FCSTD DOCUMENT  (FreeCAD 0.20R26155 (Git))
Label: helical-antenna 300-500MHz
License: All rights reserved
LicenseURL: http://en.wikipedia.org/wiki/All_rights_reserved
objects: Sketcher::SketchObject×1
note: 1 computed .brp shape members not serialized (recipe doc carries the construction recipe); baked Part::Feature solids carry a one-line shape summary decoded from their .brp

FEATURE [Sketcher::SketchObject] Sketch  label="Pads_TH_SMD"
  FullyConstrained = true
  sketch-geometry (95):
    g0: ArcOfCircle CenterX=0.508 CenterY=0.508 CenterZ=0 NormalX=0 NormalY=0 NormalZ=1 AngleXU=0 Radius=0.508 StartAngle=2.89823 EndAngle=6.03983
    g1: ArcOfCircle CenterX=1.524 CenterY=4.60016 CenterZ=0 NormalX=0 NormalY=0 NormalZ=1 AngleXU=0 Radius=0.508 StartAngle=6.03983 EndAngle=9.18142
    g2: LineSegment StartX=1.00103 StartY=0.38559 StartZ=0 EndX=2.01703 EndY=4.47775 EndZ=0
    g3: LineSegment StartX=1.03097 StartY=4.72257 StartZ=0 EndX=0.0149687 EndY=0.63041 EndZ=0
    g4: LineSegment StartX=0.38559 StartY=0.0149687 StartZ=0 EndX=1.64641 EndY=5.09319 EndZ=0
    g5: ArcOfCircle CenterX=2.54 CenterY=0.508 CenterZ=0 NormalX=0 NormalY=0 NormalZ=1 AngleXU=0 Radius=0.508 StartAngle=2.89823 EndAngle=6.03983
    g6: ArcOfCircle CenterX=3.556 CenterY=4.60016 CenterZ=0 NormalX=0 NormalY=0 NormalZ=1 AngleXU=0 Radius=0.508 StartAngle=6.03983 EndAngle=9.18142
    g7: LineSegment StartX=3.03303 StartY=0.38559 StartZ=0 EndX=4.04903 EndY=4.47775 EndZ=0
    g8: LineSegment StartX=3.06297 StartY=4.72257 StartZ=0 EndX=2.04697 EndY=0.63041 EndZ=0
    g9: LineSegment StartX=2.41759 StartY=0.0149687 StartZ=0 EndX=3.67841 EndY=5.09319 EndZ=0
    g10: LineSegment StartX=0.0149687 StartY=0.63041 StartZ=0 EndX=2.04697 EndY=0.63041 EndZ=0
    g11: ArcOfCircle CenterX=4.572 CenterY=0.508 CenterZ=0 NormalX=0 NormalY=0 NormalZ=1 AngleXU=0 Radius=0.508 StartAngle=2.89823 EndAngle=6.03983
    g12: ArcOfCircle CenterX=5.588 CenterY=4.60016 CenterZ=0 NormalX=0 NormalY=0 NormalZ=1 AngleXU=0 Radius=0.508 StartAngle=6.03983 EndAngle=9.18142
    g13: LineSegment StartX=5.06503 StartY=0.38559 StartZ=0 EndX=6.08103 EndY=4.47775 EndZ=0
    g14: LineSegment StartX=5.09497 StartY=4.72257 StartZ=0 EndX=4.07897 EndY=0.63041 EndZ=0
    g15: LineSegment StartX=4.44959 StartY=0.0149687 StartZ=0 EndX=5.71041 EndY=5.09319 EndZ=0
    g16: LineSegment StartX=2.04697 StartY=0.63041 StartZ=0 EndX=4.07897 EndY=0.63041 EndZ=0
    g17: ArcOfCircle CenterX=6.604 CenterY=0.508 CenterZ=0 NormalX=0 NormalY=0 NormalZ=1 AngleXU=0 Radius=0.508 StartAngle=2.89823 EndAngle=6.03983
    g18: ArcOfCircle CenterX=7.62 CenterY=4.60016 CenterZ=0 NormalX=0 NormalY=0 NormalZ=1 AngleXU=0 Radius=0.508 StartAngle=6.03983 EndAngle=9.18142
    g19: LineSegment StartX=7.09703 StartY=0.38559 StartZ=0 EndX=8.11303 EndY=4.47775 EndZ=0
    g20: LineSegment StartX=7.12697 StartY=4.72257 StartZ=0 EndX=6.11097 EndY=0.63041 EndZ=0
    g21: LineSegment StartX=6.48159 StartY=0.0149687 StartZ=0 EndX=7.74241 EndY=5.09319 EndZ=0
    g22: LineSegment StartX=4.07897 StartY=0.63041 StartZ=0 EndX=6.11097 EndY=0.63041 EndZ=0
    g23: ArcOfCircle CenterX=8.636 CenterY=0.508 CenterZ=0 NormalX=0 NormalY=0 NormalZ=1 AngleXU=0 Radius=0.508 StartAngle=2.89823 EndAngle=6.03983
    g24: ArcOfCircle CenterX=9.652 CenterY=4.60016 CenterZ=0 NormalX=0 NormalY=0 NormalZ=1 AngleXU=0 Radius=0.508 StartAngle=6.03983 EndAngle=9.18142
    g25: LineSegment StartX=9.12903 StartY=0.38559 StartZ=0 EndX=10.145 EndY=4.47775 EndZ=0
    g26: LineSegment StartX=9.15897 StartY=4.72257 StartZ=0 EndX=8.14297 EndY=0.63041 EndZ=0
    g27: LineSegment StartX=8.51359 StartY=0.0149687 StartZ=0 EndX=9.77441 EndY=5.09319 EndZ=0
    g28: LineSegment StartX=6.11097 StartY=0.63041 StartZ=0 EndX=8.14297 EndY=0.63041 EndZ=0
    g29: ArcOfCircle CenterX=10.668 CenterY=0.508 CenterZ=0 NormalX=0 NormalY=0 NormalZ=1 AngleXU=0 Radius=0.508 StartAngle=2.89823 EndAngle=6.03983
    g30: ArcOfCircle CenterX=11.684 CenterY=4.60016 CenterZ=0 NormalX=0 NormalY=0 NormalZ=1 AngleXU=0 Radius=0.508 StartAngle=6.03983 EndAngle=9.18142
    g31: LineSegment StartX=11.161 StartY=0.38559 StartZ=0 EndX=12.177 EndY=4.47775 EndZ=0
    g32: LineSegment StartX=11.191 StartY=4.72257 StartZ=0 EndX=10.175 EndY=0.63041 EndZ=0
    g33: LineSegment StartX=10.5456 StartY=0.0149687 StartZ=0 EndX=11.8064 EndY=5.09319 EndZ=0
    g34: LineSegment StartX=8.14297 StartY=0.63041 StartZ=0 EndX=10.175 EndY=0.63041 EndZ=0
    g35: ArcOfCircle CenterX=12.7 CenterY=0.508 CenterZ=0 NormalX=0 NormalY=0 NormalZ=1 AngleXU=0 Radius=0.508 StartAngle=2.89823 EndAngle=6.03983
    g36: ArcOfCircle CenterX=13.716 CenterY=4.60016 CenterZ=0 NormalX=0 NormalY=0 NormalZ=1 AngleXU=0 Radius=0.508 StartAngle=6.03983 EndAngle=9.18142
    g37: LineSegment StartX=13.193 StartY=0.38559 StartZ=0 EndX=14.209 EndY=4.47775 EndZ=0
    g38: LineSegment StartX=13.223 StartY=4.72257 StartZ=0 EndX=12.207 EndY=0.63041 EndZ=0
    g39: LineSegment StartX=12.5776 StartY=0.0149687 StartZ=0 EndX=13.8384 EndY=5.09319 EndZ=0
    g40: LineSegment StartX=10.175 StartY=0.63041 StartZ=0 EndX=12.207 EndY=0.63041 EndZ=0
    g41: ArcOfCircle CenterX=14.732 CenterY=0.508 CenterZ=0 NormalX=0 NormalY=0 NormalZ=1 AngleXU=0 Radius=0.508 StartAngle=2.89823 EndAngle=6.03983
    g42: ArcOfCircle CenterX=15.748 CenterY=4.60016 CenterZ=0 NormalX=0 NormalY=0 NormalZ=1 AngleXU=0 Radius=0.508 StartAngle=6.03983 EndAngle=9.18142
    g43: LineSegment StartX=15.225 StartY=0.38559 StartZ=0 EndX=16.241 EndY=4.47775 EndZ=0
    g44: LineSegment StartX=15.255 StartY=4.72257 StartZ=0 EndX=14.239 EndY=0.63041 EndZ=0
    g45: LineSegment StartX=14.6096 StartY=0.0149687 StartZ=0 EndX=15.8704 EndY=5.09319 EndZ=0
    g46: LineSegment StartX=12.207 StartY=0.63041 StartZ=0 EndX=14.239 EndY=0.63041 EndZ=0
    g47: ArcOfCircle CenterX=16.764 CenterY=0.508 CenterZ=0 NormalX=0 NormalY=0 NormalZ=1 AngleXU=0 Radius=0.508 StartAngle=2.89823 EndAngle=6.03983
    g48: ArcOfCircle CenterX=17.78 CenterY=4.60016 CenterZ=0 NormalX=0 NormalY=0 NormalZ=1 AngleXU=0 Radius=0.508 StartAngle=6.03983 EndAngle=9.18142
    g49: LineSegment StartX=17.257 StartY=0.38559 StartZ=0 EndX=18.273 EndY=4.47775 EndZ=0
    g50: LineSegment StartX=17.287 StartY=4.72257 StartZ=0 EndX=16.271 EndY=0.63041 EndZ=0
    g51: LineSegment StartX=16.6416 StartY=0.0149687 StartZ=0 EndX=17.9024 EndY=5.09319 EndZ=0
    g52: LineSegment StartX=14.239 StartY=0.63041 StartZ=0 EndX=16.271 EndY=0.63041 EndZ=0
    g53: ArcOfCircle CenterX=18.796 CenterY=0.508 CenterZ=0 NormalX=0 NormalY=0 NormalZ=1 AngleXU=0 Radius=0.508 StartAngle=2.89823 EndAngle=6.03983
    g54: ArcOfCircle CenterX=19.812 CenterY=4.60016 CenterZ=0 NormalX=0 NormalY=0 NormalZ=1 AngleXU=0 Radius=0.508 StartAngle=6.03983 EndAngle=9.18142
    g55: LineSegment StartX=19.289 StartY=0.38559 StartZ=0 EndX=20.305 EndY=4.47775 EndZ=0
    g56: LineSegment StartX=19.319 StartY=4.72257 StartZ=0 EndX=18.303 EndY=0.63041 EndZ=0
    g57: LineSegment StartX=18.6736 StartY=0.0149687 StartZ=0 EndX=19.9344 EndY=5.09319 EndZ=0
    g58: LineSegment StartX=16.271 StartY=0.63041 StartZ=0 EndX=18.303 EndY=0.63041 EndZ=0
    g59: ArcOfCircle CenterX=20.828 CenterY=0.508 CenterZ=0 NormalX=0 NormalY=0 NormalZ=1 AngleXU=0 Radius=0.508 StartAngle=2.89823 EndAngle=6.03983
    g60: ArcOfCircle CenterX=21.844 CenterY=4.60016 CenterZ=0 NormalX=0 NormalY=0 NormalZ=1 AngleXU=0 Radius=0.508 StartAngle=6.03983 EndAngle=9.18142
    g61: LineSegment StartX=21.321 StartY=0.38559 StartZ=0 EndX=22.337 EndY=4.47775 EndZ=0
    g62: LineSegment StartX=21.351 StartY=4.72257 StartZ=0 EndX=20.335 EndY=0.63041 EndZ=0
    g63: LineSegment StartX=20.7056 StartY=0.0149687 StartZ=0 EndX=21.9664 EndY=5.09319 EndZ=0
    g64: LineSegment StartX=18.303 StartY=0.63041 StartZ=0 EndX=20.335 EndY=0.63041 EndZ=0
    g65: ArcOfCircle CenterX=22.86 CenterY=0.508 CenterZ=0 NormalX=0 NormalY=0 NormalZ=1 AngleXU=0 Radius=0.508 StartAngle=2.89823 EndAngle=6.03983
    g66: ArcOfCircle CenterX=23.876 CenterY=4.60016 CenterZ=0 NormalX=0 NormalY=0 NormalZ=1 AngleXU=0 Radius=0.508 StartAngle=6.03983 EndAngle=9.18142
    g67: LineSegment StartX=23.353 StartY=0.38559 StartZ=0 EndX=24.369 EndY=4.47775 EndZ=0
    g68: LineSegment StartX=23.383 StartY=4.72257 StartZ=0 EndX=22.367 EndY=0.63041 EndZ=0
    g69: LineSegment StartX=22.7376 StartY=0.0149687 StartZ=0 EndX=23.9984 EndY=5.09319 EndZ=0
    g70: LineSegment StartX=20.335 StartY=0.63041 StartZ=0 EndX=22.367 EndY=0.63041 EndZ=0
    g71: ArcOfCircle CenterX=24.892 CenterY=0.508 CenterZ=0 NormalX=0 NormalY=0 NormalZ=1 AngleXU=0 Radius=0.508 StartAngle=2.89823 EndAngle=6.03983
    g72: ArcOfCircle CenterX=25.908 CenterY=4.60016 CenterZ=0 NormalX=0 NormalY=0 NormalZ=1 AngleXU=0 Radius=0.508 StartAngle=6.03983 EndAngle=9.18142
    g73: LineSegment StartX=25.385 StartY=0.38559 StartZ=0 EndX=26.401 EndY=4.47775 EndZ=0
    g74: LineSegment StartX=25.415 StartY=4.72257 StartZ=0 EndX=24.399 EndY=0.63041 EndZ=0
    g75: LineSegment StartX=24.7696 StartY=0.0149687 StartZ=0 EndX=26.0304 EndY=5.09319 EndZ=0
    g76: LineSegment StartX=22.367 StartY=0.63041 StartZ=0 EndX=24.399 EndY=0.63041 EndZ=0
    g77: ArcOfCircle CenterX=26.924 CenterY=0.508 CenterZ=0 NormalX=0 NormalY=0 NormalZ=1 AngleXU=0 Radius=0.508 StartAngle=2.89823 EndAngle=6.03983
    g78: ArcOfCircle CenterX=27.94 CenterY=4.60016 CenterZ=0 NormalX=0 NormalY=0 NormalZ=1 AngleXU=0 Radius=0.508 StartAngle=6.03983 EndAngle=9.18142
    g79: LineSegment StartX=27.417 StartY=0.38559 StartZ=0 EndX=28.433 EndY=4.47775 EndZ=0
    g80: LineSegment StartX=27.447 StartY=4.72257 StartZ=0 EndX=26.431 EndY=0.63041 EndZ=0
    g81: LineSegment StartX=26.8016 StartY=0.0149687 StartZ=0 EndX=28.0624 EndY=5.09319 EndZ=0
    g82: LineSegment StartX=24.399 StartY=0.63041 StartZ=0 EndX=26.431 EndY=0.63041 EndZ=0
    g83: ArcOfCircle CenterX=28.956 CenterY=0.508 CenterZ=0 NormalX=0 NormalY=0 NormalZ=1 AngleXU=0 Radius=0.508 StartAngle=2.89823 EndAngle=6.03983
    g84: ArcOfCircle CenterX=29.972 CenterY=4.60016 CenterZ=0 NormalX=0 NormalY=0 NormalZ=1 AngleXU=0 Radius=0.508 StartAngle=6.03983 EndAngle=9.18142
    g85: LineSegment StartX=29.449 StartY=0.38559 StartZ=0 EndX=30.465 EndY=4.47775 EndZ=0
    g86: LineSegment StartX=29.479 StartY=4.72257 StartZ=0 EndX=28.463 EndY=0.63041 EndZ=0
    g87: LineSegment StartX=28.8336 StartY=0.0149687 StartZ=0 EndX=30.0944 EndY=5.09319 EndZ=0
    g88: LineSegment StartX=26.431 StartY=0.63041 StartZ=0 EndX=28.463 EndY=0.63041 EndZ=0
    g89: ArcOfCircle CenterX=-0.508 CenterY=4.59084 CenterZ=0 NormalX=0 NormalY=0 NormalZ=1 AngleXU=0 Radius=0.508 StartAngle=6.13393 EndAngle=9.27553
    g90: ArcOfCircle CenterX=-1.524 CenterY=-2.1658 CenterZ=0 NormalX=0 NormalY=0 NormalZ=1 AngleXU=0 Radius=0.508 StartAngle=2.99234 EndAngle=6.13393
    g91: LineSegment StartX=-1.01035 StartY=4.66638 StartZ=0 EndX=-2.02635 EndY=-2.09026 EndZ=0
    g92: LineSegment StartX=-1.02165 StartY=-2.24134 StartZ=0 EndX=-0.00564768 EndY=4.5153 EndZ=0
    g93: LineSegment StartX=-1.59954 StartY=-2.66815 StartZ=0 EndX=-0.432461 EndY=5.09319 EndZ=0
    g94: LineSegment StartX=-0.432461 StartY=5.09319 StartZ=0 EndX=1.64641 EndY=5.09319 EndZ=0
  constraints (254):
    c: Tangent(g0,g2) = -1.5708
    c: Tangent(g2,g1) = -1.5708
    c: Tangent(g1,g3) = -1.5708
    c: Tangent(g3,g0) = -1.5708
    c: Equal(g0,g1)
    c: PointOnObject(g4,g0)
    c: PointOnObject(g4,g1)
    c: PointOnObject(g1,g4)
    c: PointOnObject(g0,g4)
    c: Distance(g4) = 5.2324
    c: Distance(g1,g1) = 1.016
    c: DistanceX(g0,g1) = 1.016
    c: Tangent(g5,g7) = -1.5708
    c: Tangent(g7,g6) = -1.5708
    c: Tangent(g6,g8) = -1.5708
    c: Tangent(g8,g5) = -1.5708
    c: Equal(g5,g6)
    c: PointOnObject(g9,g5)
    c: PointOnObject(g9,g6)
    c: PointOnObject(g6,g9)
    c: PointOnObject(g5,g9)
    c: Equal(g4,g9) = 5.2324
    c: Equal(g1,g6) = 1.016
    c: DistanceX(g5,g6) = 1.016
    c: Coincident(g0,g10)
    c: Coincident(g5,g10)
    c: Distance(g10) = 2.032
    c: Angle(g10) = 0
    c: Tangent(g11,g13) = -1.5708
    c: Tangent(g13,g12) = -1.5708
    c: Tangent(g12,g14) = -1.5708
    c: Tangent(g14,g11) = -1.5708
    c: Equal(g11,g12)
    c: PointOnObject(g15,g11)
    c: PointOnObject(g15,g12)
    c: PointOnObject(g12,g15)
    c: PointOnObject(g11,g15)
    c: Equal(g4,g15) = 5.2324
    c: Equal(g1,g12) = 1.016
    c: DistanceX(g11,g12) = 1.016
    c: Coincident(g5,g16)
    c: Coincident(g11,g16)
    c: Equal(g10,g16)
    c: Parallel(g16,g10)
    c: Tangent(g17,g19) = -1.5708
    c: Tangent(g19,g18) = -1.5708
    c: Tangent(g18,g20) = -1.5708
    c: Tangent(g20,g17) = -1.5708
    c: Equal(g17,g18)
    c: PointOnObject(g21,g17)
    c: PointOnObject(g21,g18)
    c: PointOnObject(g18,g21)
    c: PointOnObject(g17,g21)
    c: Equal(g4,g21) = 5.2324
    c: Equal(g1,g18) = 1.016
    c: DistanceX(g17,g18) = 1.016
    c: Coincident(g11,g22)
    c: Coincident(g17,g22)
    c: Equal(g10,g22)
    c: Parallel(g22,g10)
    c: Tangent(g23,g25) = -1.5708
    c: Tangent(g25,g24) = -1.5708
    c: Tangent(g24,g26) = -1.5708
    c: Tangent(g26,g23) = -1.5708
    c: Equal(g23,g24)
    c: PointOnObject(g27,g23)
    c: PointOnObject(g27,g24)
    c: PointOnObject(g24,g27)
    c: PointOnObject(g23,g27)
    c: Equal(g4,g27) = 5.2324
    c: Equal(g1,g24) = 1.016
    c: DistanceX(g23,g24) = 1.016
    c: Coincident(g17,g28)
    c: Coincident(g23,g28)
    c: Equal(g10,g28)
    c: Parallel(g28,g10)
    c: Tangent(g29,g31) = -1.5708
    c: Tangent(g31,g30) = -1.5708
    c: Tangent(g30,g32) = -1.5708
    c: Tangent(g32,g29) = -1.5708
    c: Equal(g29,g30)
    c: PointOnObject(g33,g29)
    c: PointOnObject(g33,g30)
    c: PointOnObject(g30,g33)
    c: PointOnObject(g29,g33)
    c: Equal(g4,g33) = 5.2324
    c: Equal(g1,g30) = 1.016
    c: DistanceX(g29,g30) = 1.016
    c: Coincident(g23,g34)
    c: Coincident(g29,g34)
    c: Equal(g10,g34)
    c: Parallel(g34,g10)
    c: Tangent(g35,g37) = -1.5708
    c: Tangent(g37,g36) = -1.5708
    c: Tangent(g36,g38) = -1.5708
    c: Tangent(g38,g35) = -1.5708
    c: Equal(g35,g36)
    c: PointOnObject(g39,g35)
    c: PointOnObject(g39,g36)
    c: PointOnObject(g36,g39)
    c: PointOnObject(g35,g39)
    c: Equal(g4,g39) = 5.2324
    c: Equal(g1,g36) = 1.016
    c: DistanceX(g35,g36) = 1.016
    c: Coincident(g29,g40)
    c: Coincident(g35,g40)
    c: Equal(g10,g40)
    c: Parallel(g40,g10)
    c: Tangent(g41,g43) = -1.5708
    c: Tangent(g43,g42) = -1.5708
    c: Tangent(g42,g44) = -1.5708
    c: Tangent(g44,g41) = -1.5708
    c: Equal(g41,g42)
    c: PointOnObject(g45,g41)
    c: PointOnObject(g45,g42)
    c: PointOnObject(g42,g45)
    c: PointOnObject(g41,g45)
    c: Equal(g4,g45) = 5.2324
    c: Equal(g1,g42) = 1.016
    c: DistanceX(g41,g42) = 1.016
    c: Coincident(g35,g46)
    c: Coincident(g41,g46)
    c: Equal(g10,g46)
    c: Parallel(g46,g10)
    c: Tangent(g47,g49) = -1.5708
    c: Tangent(g49,g48) = -1.5708
    c: Tangent(g48,g50) = -1.5708
    c: Tangent(g50,g47) = -1.5708
    c: Equal(g47,g48)
    c: PointOnObject(g51,g47)
    c: PointOnObject(g51,g48)
    c: PointOnObject(g48,g51)
    c: PointOnObject(g47,g51)
    c: Equal(g4,g51) = 5.2324
    c: Equal(g1,g48) = 1.016
    c: DistanceX(g47,g48) = 1.016
    c: Coincident(g41,g52)
    c: Coincident(g47,g52)
    c: Equal(g10,g52)
    c: Parallel(g52,g10)
    c: Tangent(g53,g55) = -1.5708
    c: Tangent(g55,g54) = -1.5708
    c: Tangent(g54,g56) = -1.5708
    c: Tangent(g56,g53) = -1.5708
    c: Equal(g53,g54)
    c: PointOnObject(g57,g53)
    c: PointOnObject(g57,g54)
    c: PointOnObject(g54,g57)
    c: PointOnObject(g53,g57)
    c: Equal(g4,g57) = 5.2324
    c: Equal(g1,g54) = 1.016
    c: DistanceX(g53,g54) = 1.016
    c: Coincident(g47,g58)
    c: Coincident(g53,g58)
    c: Equal(g10,g58)
    c: Parallel(g58,g10)
    c: Tangent(g59,g61) = -1.5708
    c: Tangent(g61,g60) = -1.5708
    c: Tangent(g60,g62) = -1.5708
    c: Tangent(g62,g59) = -1.5708
    c: Equal(g59,g60)
    c: PointOnObject(g63,g59)
    c: PointOnObject(g63,g60)
    c: PointOnObject(g60,g63)
    c: PointOnObject(g59,g63)
    c: Equal(g4,g63) = 5.2324
    c: Equal(g1,g60) = 1.016
    c: DistanceX(g59,g60) = 1.016
    c: Coincident(g53,g64)
    c: Coincident(g59,g64)
    c: Equal(g10,g64)
    c: Parallel(g64,g10)
    c: Tangent(g65,g67) = -1.5708
    c: Tangent(g67,g66) = -1.5708
    c: Tangent(g66,g68) = -1.5708
    c: Tangent(g68,g65) = -1.5708
    c: Equal(g65,g66)
    c: PointOnObject(g69,g65)
    c: PointOnObject(g69,g66)
    c: PointOnObject(g66,g69)
    c: PointOnObject(g65,g69)
    c: Equal(g4,g69) = 5.2324
    c: Equal(g1,g66) = 1.016
    c: DistanceX(g65,g66) = 1.016
    c: Coincident(g59,g70)
    c: Coincident(g65,g70)
    c: Equal(g10,g70)
    c: Parallel(g70,g10)
    c: Tangent(g71,g73) = -1.5708
    c: Tangent(g73,g72) = -1.5708
    c: Tangent(g72,g74) = -1.5708
    c: Tangent(g74,g71) = -1.5708
    c: Equal(g71,g72)
    c: PointOnObject(g75,g71)
    c: PointOnObject(g75,g72)
    c: PointOnObject(g72,g75)
    c: PointOnObject(g71,g75)
    c: Equal(g4,g75) = 5.2324
    c: Equal(g1,g72) = 1.016
    c: DistanceX(g71,g72) = 1.016
    c: Coincident(g65,g76)
    c: Coincident(g71,g76)
    c: Equal(g10,g76)
    c: Parallel(g76,g10)
    c: Tangent(g77,g79) = -1.5708
    c: Tangent(g79,g78) = -1.5708
    c: Tangent(g78,g80) = -1.5708
    c: Tangent(g80,g77) = -1.5708
    c: Equal(g77,g78)
    c: PointOnObject(g81,g77)
    c: PointOnObject(g81,g78)
    c: PointOnObject(g78,g81)
    c: PointOnObject(g77,g81)
    c: Equal(g4,g81) = 5.2324
    c: Equal(g1,g78) = 1.016
    c: DistanceX(g77,g78) = 1.016
    c: Coincident(g71,g82)
    c: Coincident(g77,g82)
    c: Equal(g10,g82)
    c: Parallel(g82,g10)
    c: Tangent(g83,g85) = -1.5708
    c: Tangent(g85,g84) = -1.5708
    c: Tangent(g84,g86) = -1.5708
    c: Tangent(g86,g83) = -1.5708
    c: Equal(g83,g84)
    c: PointOnObject(g87,g83)
    c: PointOnObject(g87,g84)
    c: PointOnObject(g84,g87)
    c: PointOnObject(g83,g87)
    c: Equal(g4,g87) = 5.2324
    c: Equal(g1,g84) = 1.016
    c: DistanceX(g83,g84) = 1.016
    c: Coincident(g77,g88)
    c: Coincident(g83,g88)
    c: Equal(g10,g88)
    c: Parallel(g88,g10)
    c: Tangent(g0,g-1)
    c: Tangent(g0,g-2)
    c: Tangent(g89,g91) = -1.5708
    c: Tangent(g91,g90) = -1.5708
    c: Tangent(g90,g92) = -1.5708
    c: Tangent(g92,g89) = -1.5708
    c: Equal(g89,g90)
    c: Distance(g89,g89) = 1.016
    c: DistanceX(g89,g0) = 1.016
    c: PointOnObject(g93,g90)
    c: PointOnObject(g93,g89)
    c: PointOnObject(g89,g93)
    c: PointOnObject(g90,g93)
    c: Distance(g93) = 7.8486
    c: Coincident(g94,g93)
    c: Coincident(g94,g4)
    c: Horizontal(g94)
    c: DistanceX(g90,g89) = 1.016
